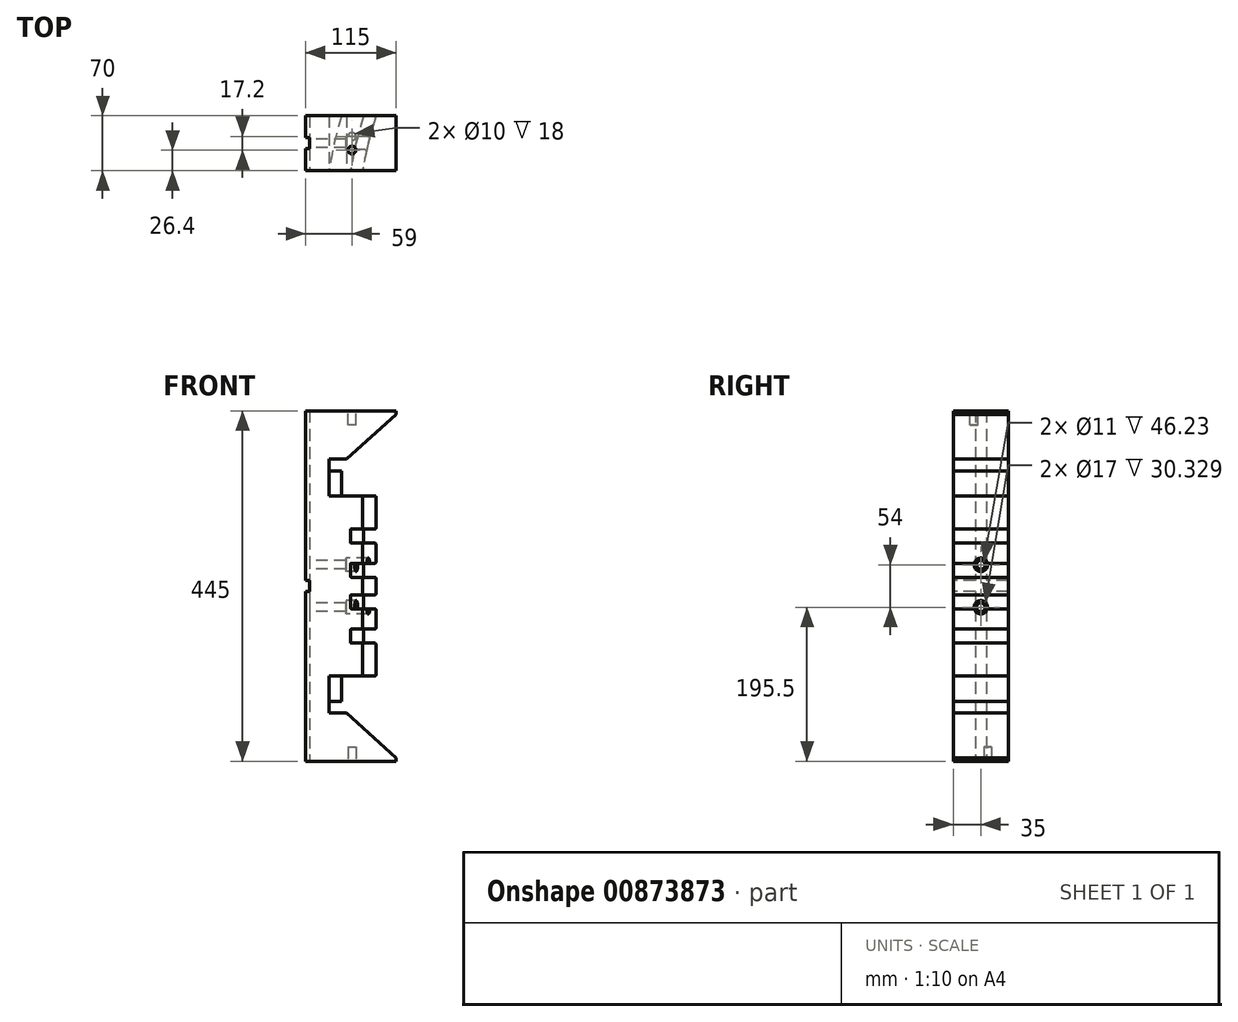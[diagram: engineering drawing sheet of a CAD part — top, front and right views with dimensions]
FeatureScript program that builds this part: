
annotation { "Feature Type Name" : "Feature", "Feature Type Description" : "" }
export const myFeature = defineFeature(function(context is Context, id is Id, definition is map)
    precondition{}
    {
        {
            var Q0;
            Q0=qCreatedBy(makeId("Top.planeOp"),FACE);
            var sketch = newSketch(context, id + "F0", { "sketchPlane" : qUnion([Q0])});
            skArc(sketch, "E0", {"start": v(-433.01, 250) * mm, "mid": v(-482.96, 129.4) * mm, "end": v(-500, 0) * mm});
            skLineSegment(sketch, "E1", {"start": v(0, 0) * mm, "end": v(-433.01, 250) * mm, "construction": true});
            skLineSegment(sketch, "E2", {"start": v(0, 0) * mm, "end": v(-500, 0) * mm, "construction": true});
            skSolve(sketch);
        }
        {
            var Q0;
            Q0=qCreatedBy(makeId("Front.planeOp"),FACE);
            var sketch = newSketch(context, id + "F1", { "sketchPlane" : qUnion([Q0])});
            skLineSegment(sketch, "E3", {"start": v(-500, 0) * mm, "end": v(-500, 9.2) * mm});
            skLineSegment(sketch, "E4", {"start": v(-502, 11.2) * mm, "end": v(-514, 11.2) * mm});
            skLineSegment(sketch, "E5", {"start": v(-515, 12.2) * mm, "end": v(-515, 27.9) * mm});
            skLineSegment(sketch, "E6", {"start": v(-514, 28.9) * mm, "end": v(-502, 28.9) * mm});
            skLineSegment(sketch, "E7", {"start": v(-502, 72.44) * mm, "end": v(-514, 72.44) * mm});
            skLineSegment(sketch, "E8", {"start": v(-515, 55.66) * mm, "end": v(-515, 71.44) * mm});
            skLineSegment(sketch, "E9", {"start": v(-514, 54.66) * mm, "end": v(-502.1, 54.66) * mm});
            skLineSegment(sketch, "E10", {"start": v(-502, 114.4) * mm, "end": v(-542, 114.4) * mm});
            skLineSegment(sketch, "E11", {"start": v(-542, 114.4) * mm, "end": v(-542, 146.4) * mm});
            skLineSegment(sketch, "E12", {"start": v(-542, 146.4) * mm, "end": v(-565, 146.4) * mm});
            skLineSegment(sketch, "E13", {"start": v(-565, 146.4) * mm, "end": v(-565, 0) * mm});
            skLineSegment(sketch, "E14", {"start": v(-515, 63.55) * mm, "end": v(-448.96, 63.55) * mm, "construction": true});
            skLineSegment(sketch, "E15", {"start": v(-515, 20.05) * mm, "end": v(-458.8, 20.05) * mm, "construction": true});
            skLineSegment(sketch, "E16", {"start": v(-500, 112.4) * mm, "end": v(-500, 74.44) * mm});
            skLineSegment(sketch, "E17", {"start": v(-500, 52.56) * mm, "end": v(-500, 30.9) * mm});
            skPoint(sketch, "E18.visualSharp", {"position": v(-515, 72.44) * mm});
            skArc(sketch, "E18.filletArc", {"start": v(-514, 72.44) * mm, "mid": v(-514.7, 72.15) * mm, "end": v(-515, 71.44) * mm});
            skPoint(sketch, "E19.visualSharp", {"position": v(-515, 54.66) * mm});
            skArc(sketch, "E19.filletArc", {"start": v(-515, 55.66) * mm, "mid": v(-514.7, 54.95) * mm, "end": v(-514, 54.66) * mm});
            skPoint(sketch, "E20.visualSharp", {"position": v(-515, 28.9) * mm});
            skArc(sketch, "E20.filletArc", {"start": v(-514, 28.9) * mm, "mid": v(-514.7, 28.6) * mm, "end": v(-515, 27.9) * mm});
            skPoint(sketch, "E21.visualSharp", {"position": v(-515, 11.2) * mm});
            skArc(sketch, "E21.filletArc", {"start": v(-515, 12.2) * mm, "mid": v(-514.7, 11.5) * mm, "end": v(-514, 11.2) * mm});
            skPoint(sketch, "E22.visualSharp", {"position": v(-500, 11.2) * mm});
            skArc(sketch, "E22.filletArc", {"start": v(-500, 9.2) * mm, "mid": v(-500.59, 10.61) * mm, "end": v(-502, 11.2) * mm});
            skPoint(sketch, "E23.visualSharp", {"position": v(-500, 28.9) * mm});
            skArc(sketch, "E23.filletArc", {"start": v(-502, 28.9) * mm, "mid": v(-500.59, 29.49) * mm, "end": v(-500, 30.9) * mm});
            skPoint(sketch, "E24.visualSharp", {"position": v(-500, 54.66) * mm});
            skArc(sketch, "E24.filletArc", {"start": v(-500, 52.56) * mm, "mid": v(-500.62, 54.04) * mm, "end": v(-502.1, 54.66) * mm});
            skPoint(sketch, "E25.visualSharp", {"position": v(-500, 72.44) * mm});
            skArc(sketch, "E25.filletArc", {"start": v(-502, 72.44) * mm, "mid": v(-500.59, 73.03) * mm, "end": v(-500, 74.44) * mm});
            skPoint(sketch, "E26.visualSharp", {"position": v(-500, 114.4) * mm});
            skArc(sketch, "E26.filletArc", {"start": v(-500, 112.4) * mm, "mid": v(-500.59, 113.81) * mm, "end": v(-502, 114.4) * mm});
            skArc(sketch, "E27.MirrorCS", {"start": v(-500, -9.2) * mm, "mid": v(-500.59, -10.61) * mm, "end": v(-502, -11.2) * mm});
            skLineSegment(sketch, "E28.MirrorCS", {"start": v(-502, -11.2) * mm, "end": v(-514, -11.2) * mm});
            skLineSegment(sketch, "E29.MirrorCS", {"start": v(-502, -72.44) * mm, "end": v(-514, -72.44) * mm});
            skArc(sketch, "E30.MirrorCS", {"start": v(-502, -72.44) * mm, "mid": v(-500.59, -73.03) * mm, "end": v(-500, -74.44) * mm});
            skArc(sketch, "E31.MirrorCS", {"start": v(-514, -72.44) * mm, "mid": v(-514.7, -72.15) * mm, "end": v(-515, -71.44) * mm});
            skArc(sketch, "E32.MirrorCS", {"start": v(-515, -12.2) * mm, "mid": v(-514.7, -11.5) * mm, "end": v(-514, -11.2) * mm});
            skArc(sketch, "E33.MirrorCS", {"start": v(-514, -28.9) * mm, "mid": v(-514.7, -28.6) * mm, "end": v(-515, -27.9) * mm});
            skArc(sketch, "E34.MirrorCS", {"start": v(-500, -112.4) * mm, "mid": v(-500.59, -113.81) * mm, "end": v(-502, -114.4) * mm});
            skLineSegment(sketch, "E35.MirrorCS", {"start": v(-514, -54.66) * mm, "end": v(-502.1, -54.66) * mm});
            skLineSegment(sketch, "E36.MirrorCS", {"start": v(-515, -55.66) * mm, "end": v(-515, -71.44) * mm});
            skArc(sketch, "E37.MirrorCS", {"start": v(-502, -28.9) * mm, "mid": v(-500.59, -29.49) * mm, "end": v(-500, -30.9) * mm});
            skLineSegment(sketch, "E38.MirrorCS", {"start": v(-514, -28.9) * mm, "end": v(-502, -28.9) * mm});
            skArc(sketch, "E39.MirrorCS", {"start": v(-500, -52.56) * mm, "mid": v(-500.62, -54.04) * mm, "end": v(-502.1, -54.66) * mm});
            skArc(sketch, "E40.MirrorCS", {"start": v(-515, -55.66) * mm, "mid": v(-514.7, -54.95) * mm, "end": v(-514, -54.66) * mm});
            skLineSegment(sketch, "E41.MirrorCS", {"start": v(-515, -12.2) * mm, "end": v(-515, -27.9) * mm});
            skPoint(sketch, "E42.MirrorP", {"position": v(-500, -11.2) * mm});
            skPoint(sketch, "E43.MirrorP", {"position": v(-500, -72.44) * mm});
            skPoint(sketch, "E44.MirrorP", {"position": v(-515, -11.2) * mm});
            skPoint(sketch, "E45.MirrorP", {"position": v(-500, -28.9) * mm});
            skPoint(sketch, "E46.MirrorP", {"position": v(-500, -54.66) * mm});
            skLineSegment(sketch, "E47.MirrorCS", {"start": v(-500, -52.56) * mm, "end": v(-500, -30.9) * mm});
            skPoint(sketch, "E48.MirrorP", {"position": v(-515, -72.44) * mm});
            skPoint(sketch, "E49.MirrorP", {"position": v(-515, -28.9) * mm});
            skLineSegment(sketch, "E50.MirrorCS", {"start": v(-542, -114.4) * mm, "end": v(-542, -146.4) * mm});
            skPoint(sketch, "E51.MirrorP", {"position": v(-500, -114.4) * mm});
            skLineSegment(sketch, "E52.MirrorCS", {"start": v(-500, -112.4) * mm, "end": v(-500, -74.44) * mm});
            skLineSegment(sketch, "E53.MirrorCS", {"start": v(-542, -146.4) * mm, "end": v(-565, -146.4) * mm});
            skLineSegment(sketch, "E54.MirrorCS", {"start": v(-502, -114.4) * mm, "end": v(-542, -114.4) * mm});
            skLineSegment(sketch, "E55.MirrorCS", {"start": v(-515, -63.55) * mm, "end": v(-448.96, -63.55) * mm, "construction": true});
            skLineSegment(sketch, "E56.MirrorCS", {"start": v(-515, -20.05) * mm, "end": v(-458.8, -20.05) * mm, "construction": true});
            skLineSegment(sketch, "E57.MirrorCS", {"start": v(-565, -146.4) * mm, "end": v(-565, 0) * mm});
            skPoint(sketch, "E58.MirrorP", {"position": v(-515, -54.66) * mm});
            skLineSegment(sketch, "E59", {"start": v(-500, -9.2) * mm, "end": v(-500, 0) * mm});
            skSolve(sketch);
        }
        {
            var Q0;
            Q0=makeQuery(id+"F1.imprint","IMPRINT",FACE,{"disambiguationData":[TD([[makeQuery(id+"F1.imprint","IMPRINT",EDGE,{"derivedFrom":sQuery(id+"F1.wireOp",EDGE,"E3")}),1.0]])]});
            var Q1;
            Q1=sQuery(id+"F0.wireOp",EDGE,"E0");
            sweep(context, id + "F2", {"profiles" : qUnion([Q0]), "path" : qUnion([Q1])});
        }
        {
            var Q0;
            Q0=makeQuery(id+"F2.opSweep","SWEPT_FACE",FACE,{"disambiguationData":[OSD([sQuery(id+"F0.wireOp",EDGE,"E0"),sQuery(id+"F1.wireOp",EDGE,"E12")])]});
            var sketch = newSketch(context, id + "F3", { "sketchPlane" : qUnion([Q0])});
            skLineSegment(sketch, "E60", {"start": v(0, 0) * mm, "end": v(-565, 0) * mm});
            skLineSegment(sketch, "E61", {"start": v(-565, 85) * mm, "end": v(-565, 155) * mm});
            skLineSegment(sketch, "E62", {"start": v(-565, 85) * mm, "end": v(-558.57, 85) * mm});
            skLineSegment(sketch, "E63", {"start": v(-543.32, 155) * mm, "end": v(-565, 155) * mm});
            skArc(sketch, "E64", {"start": v(-543.32, 155) * mm, "mid": v(-552.06, 120.24) * mm, "end": v(-558.57, 85) * mm});
            skSolve(sketch);
        }
        {
            var Q0;
            Q0=makeQuery(id+"F3.imprint","IMPRINT",FACE,{"disambiguationData":[TD([[makeQuery(id+"F3.imprint","IMPRINT",EDGE,{"derivedFrom":sQuery(id+"F3.wireOp",EDGE,"E61")}),-1.0]])]});
            var Q1;
            Q1=makeQuery(id+"F2.opSweep","SWEPT_FACE",FACE,{"disambiguationData":[OSD([sQuery(id+"F0.wireOp",EDGE,"E0"),sQuery(id+"F1.wireOp",EDGE,"E53.MirrorCS")])]});
            extrude(context, id + "F4", {"entities" : qUnion([Q0]), "operationType" : NewBodyOperationType.ADD, "endBound" : BoundingType.UP_TO_SURFACE, "oppositeDirection" : true, "depth" : 25 * mm, "endBoundEntityFace" : qUnion([Q1]), "offsetDistance" : 25 * mm});
        }
        {
            var Q0;
            Q0=makeQuery(id+"F4.boolean.opBoolean","MERGE",FACE,{"derivedFrom":[makeQuery(id+"F2.opSweep","SWEPT_FACE",FACE,{"disambiguationData":[OSD([sQuery(id+"F0.wireOp",EDGE,"E0"),sQuery(id+"F1.wireOp",EDGE,"E12")])]}),makeQuery(id+"F4.opExtrude","CAP_FACE",FACE,{"disambiguationData":[OSD([sQuery(id+"F3.wireOp",EDGE,"E61"),sQuery(id+"F3.wireOp",EDGE,"E62"),sQuery(id+"F3.wireOp",EDGE,"E63"),sQuery(id+"F3.wireOp",EDGE,"E64")])],"isStart":true})]});
            var sketch = newSketch(context, id + "F5", { "sketchPlane" : qUnion([Q0])});
            skLineSegment(sketch, "E65", {"start": v(-543.32, 155) * mm, "end": v(-475.37, 155) * mm});
            skLineSegment(sketch, "E66", {"start": v(-558.57, 85) * mm, "end": v(-492.72, 85) * mm});
            skLineSegment(sketch, "E67", {"start": v(-489.3, 282.5) * mm, "end": v(-433.01, 250) * mm});
            skLineSegment(sketch, "E68", {"start": v(-565, 0) * mm, "end": v(-500, 0) * mm});
            skArc(sketch, "E69", {"start": v(-489.3, 282.5) * mm, "mid": v(-520.23, 220.41) * mm, "end": v(-543.32, 155) * mm});
            skArc(sketch, "E70", {"start": v(-433.01, 250) * mm, "mid": v(-456.67, 203.6) * mm, "end": v(-475.37, 155) * mm});
            skArc(sketch, "E71.trimOffspring", {"start": v(-492.72, 85) * mm, "mid": v(-498.18, 42.66) * mm, "end": v(-500, 0) * mm});
            skArc(sketch, "E72.trimOffspring", {"start": v(-558.57, 85) * mm, "mid": v(-563.4, 42.62) * mm, "end": v(-565, 0) * mm});
            skSolve(sketch);
        }
        {
            var Q0;
            {var subQ0=sQuery(id+"F5.wireOp",EDGE,"E71.trimOffspring");Q0=makeQuery(id+"F5.imprint","IMPRINT",FACE,{"disambiguationData":[TD([[makeQuery(id+"F5.imprint","IMPRINT",EDGE,{"derivedFrom":subQ0}),-1.0]])]});}
            var Q1;
            {var subQ0=sQuery(id+"F5.wireOp",EDGE,"E72.trimOffspring");Q1=makeQuery(id+"F5.imprint","IMPRINT",FACE,{"disambiguationData":[TD([[makeQuery(id+"F5.imprint","IMPRINT",EDGE,{"derivedFrom":subQ0}),-1.0]])]});}
            var Q2;
            {var subQ0=sQuery(id+"F5.wireOp",EDGE,"E69");Q2=makeQuery(id+"F5.imprint","IMPRINT",FACE,{"disambiguationData":[TD([[makeQuery(id+"F5.imprint","IMPRINT",EDGE,{"derivedFrom":subQ0}),-1.0]])]});}
            var Q3;
            {var subQ0=sQuery(id+"F5.wireOp",EDGE,"E70");Q3=makeQuery(id+"F5.imprint","IMPRINT",FACE,{"disambiguationData":[TD([[makeQuery(id+"F5.imprint","IMPRINT",EDGE,{"derivedFrom":subQ0}),-1.0]])]});}
            var Q4;
            Q4=makeQuery(id+"F4.boolean.opBoolean","MERGE",FACE,{"derivedFrom":[makeQuery(id+"F2.opSweep","SWEPT_FACE",FACE,{"disambiguationData":[OSD([sQuery(id+"F0.wireOp",EDGE,"E0"),sQuery(id+"F1.wireOp",EDGE,"E53.MirrorCS")])]}),makeQuery(id+"F4.opExtrude","CAP_FACE",FACE,{"disambiguationData":[OSD([sQuery(id+"F3.wireOp",EDGE,"E61"),sQuery(id+"F3.wireOp",EDGE,"E62"),sQuery(id+"F3.wireOp",EDGE,"E63"),sQuery(id+"F3.wireOp",EDGE,"E64")])],"isStart":false})]});
            extrude(context, id + "F6", {"entities" : qUnion([Q0, Q1, Q2, Q3]), "operationType" : NewBodyOperationType.REMOVE, "endBound" : BoundingType.UP_TO_SURFACE, "oppositeDirection" : true, "depth" : 25 * mm, "endBoundEntityFace" : qUnion([Q4]), "offsetDistance" : 25 * mm});
        }
        {
            var Q0;
            Q0=makeQuery(id+"F6.boolean.opBoolean","MERGE",FACE,{"derivedFrom":[makeQuery(id+"F4.opExtrude","SWEPT_FACE",FACE,{"disambiguationData":[OSD([sQuery(id+"F3.wireOp",EDGE,"E62")])]})],"fromTools":[makeQuery(id+"F6.opExtrude","SWEPT_FACE",FACE,{"disambiguationData":[OSD([sQuery(id+"F5.wireOp",EDGE,"E66")])]})]});
            var sketch = newSketch(context, id + "F7", { "sketchPlane" : qUnion([Q0])});
            skLineSegment(sketch, "E73", {"start": v(-565, 146.4) * mm, "end": v(-565, 222.5) * mm});
            skLineSegment(sketch, "E74", {"start": v(-565, 222.5) * mm, "end": v(-445, 222.5) * mm, "construction": true});
            skLineSegment(sketch, "E75", {"start": v(-445, 222.5) * mm, "end": v(-512.86, 161.4) * mm, "construction": true});
            skLineSegment(sketch, "E76", {"start": v(-512.86, 161.4) * mm, "end": v(-535.3, 161.4) * mm});
            skLineSegment(sketch, "E77", {"start": v(-535.3, 161.4) * mm, "end": v(-535.3, 146.4) * mm});
            skLineSegment(sketch, "E78", {"start": v(-535.3, 146.4) * mm, "end": v(-565, 146.4) * mm});
            skLineSegment(sketch, "E79", {"start": v(-565, 222.5) * mm, "end": v(-450, 222.5) * mm});
            skLineSegment(sketch, "E80", {"start": v(-450, 222.5) * mm, "end": v(-450, 218) * mm});
            skLineSegment(sketch, "E81", {"start": v(-512.86, 161.4) * mm, "end": v(-450, 218) * mm});
            skLineSegment(sketch, "E82.MirrorCS", {"start": v(-450, -222.5) * mm, "end": v(-450, -218) * mm});
            skLineSegment(sketch, "E83.MirrorCS", {"start": v(-535.3, -161.4) * mm, "end": v(-535.3, -146.4) * mm});
            skLineSegment(sketch, "E84.MirrorCS", {"start": v(-535.3, -146.4) * mm, "end": v(-565, -146.4) * mm});
            skLineSegment(sketch, "E85.MirrorCS", {"start": v(-512.86, -161.4) * mm, "end": v(-535.3, -161.4) * mm});
            skLineSegment(sketch, "E86.MirrorCS", {"start": v(-565, -222.5) * mm, "end": v(-450, -222.5) * mm});
            skLineSegment(sketch, "E87.MirrorCS", {"start": v(-512.86, -161.4) * mm, "end": v(-450, -218) * mm});
            skLineSegment(sketch, "E88.MirrorCS", {"start": v(-565, -222.5) * mm, "end": v(-445, -222.5) * mm, "construction": true});
            skLineSegment(sketch, "E89.MirrorCS", {"start": v(-445, -222.5) * mm, "end": v(-512.86, -161.4) * mm, "construction": true});
            skLineSegment(sketch, "E90.MirrorCS", {"start": v(-565, -146.4) * mm, "end": v(-565, -222.5) * mm});
            skSolve(sketch);
        }
        {
            var Q0;
            Q0=makeQuery(id+"F7.imprint","IMPRINT",FACE,{"disambiguationData":[TD([[makeQuery(id+"F7.imprint","IMPRINT",EDGE,{"derivedFrom":sQuery(id+"F7.wireOp",EDGE,"E82.MirrorCS")}),1.0]])]});
            var Q1;
            Q1=makeQuery(id+"F7.imprint","IMPRINT",FACE,{"disambiguationData":[TD([[makeQuery(id+"F7.imprint","IMPRINT",EDGE,{"derivedFrom":sQuery(id+"F7.wireOp",EDGE,"E73")}),-1.0]])]});
            var Q2;
            Q2=makeQuery(id+"F6.boolean.opBoolean","MERGE",FACE,{"derivedFrom":[makeQuery(id+"F4.opExtrude","SWEPT_FACE",FACE,{"disambiguationData":[OSD([sQuery(id+"F3.wireOp",EDGE,"E63")])]})],"fromTools":[makeQuery(id+"F6.opExtrude","SWEPT_FACE",FACE,{"disambiguationData":[OSD([sQuery(id+"F5.wireOp",EDGE,"E65")])]})]});
            extrude(context, id + "F8", {"entities" : qUnion([Q0, Q1]), "operationType" : NewBodyOperationType.ADD, "endBound" : BoundingType.UP_TO_SURFACE, "oppositeDirection" : true, "depth" : 25 * mm, "endBoundEntityFace" : qUnion([Q2]), "offsetDistance" : 25 * mm});
        }
        {
            var Q0;
            Q0=makeQuery(id+"F8.boolean.opBoolean","MERGE",FACE,{"derivedFrom":[makeQuery(id+"F4.opExtrude","SWEPT_FACE",FACE,{"disambiguationData":[OSD([sQuery(id+"F3.wireOp",EDGE,"E61")])]}),makeQuery(id+"F8.opExtrude","SWEPT_FACE",FACE,{"disambiguationData":[OSD([sQuery(id+"F7.wireOp",EDGE,"E73")])]}),makeQuery(id+"F8.opExtrude","SWEPT_FACE",FACE,{"disambiguationData":[OSD([sQuery(id+"F7.wireOp",EDGE,"E90.MirrorCS")])]})]});
            var sketch = newSketch(context, id + "F9", { "sketchPlane" : qUnion([Q0])});
            skLineSegment(sketch, "E91.bottom", {"start": v(-127, 222.5) * mm, "end": v(-113, 222.5) * mm});
            skLineSegment(sketch, "E91.top", {"start": v(-127, -222.5) * mm, "end": v(-113, -222.5) * mm});
            skLineSegment(sketch, "E91.left", {"start": v(-127, 222.5) * mm, "end": v(-127, 7) * mm});
            skLineSegment(sketch, "E91.right", {"start": v(-113, 222.5) * mm, "end": v(-113, 7) * mm});
            skLineSegment(sketch, "E92.bottom", {"start": v(-155, 7) * mm, "end": v(-127, 7) * mm});
            skLineSegment(sketch, "E92.top", {"start": v(-155, -7) * mm, "end": v(-127, -7) * mm});
            skLineSegment(sketch, "E92.left", {"start": v(-155, 7) * mm, "end": v(-155, -7) * mm});
            skLineSegment(sketch, "E92.right", {"start": v(-85, 7) * mm, "end": v(-85, -7) * mm});
            skLineSegment(sketch, "E93.trimOffspring", {"start": v(-113, 7) * mm, "end": v(-85, 7) * mm});
            skLineSegment(sketch, "E94.trimOffspring", {"start": v(-113, -7) * mm, "end": v(-113, -222.5) * mm});
            skLineSegment(sketch, "E95.trimOffspring", {"start": v(-113, -7) * mm, "end": v(-85, -7) * mm});
            skLineSegment(sketch, "E96.trimOffspring", {"start": v(-127, -7) * mm, "end": v(-127, -222.5) * mm});
            skSolve(sketch);
        }
        {
            var Q0;
            Q0 = qSketchRegion(id + "F9", true);
            extrude(context, id + "F10", {"entities" : qUnion([Q0]), "operationType" : NewBodyOperationType.REMOVE, "oppositeDirection" : true, "depth" : 5 * mm, "offsetDistance" : 25 * mm});
        }
        {
            var Q0;
            Q0=makeQuery(id+"F10.boolean.opBoolean","COPY",FACE,{"derivedFrom":makeQuery(id+"F10.opExtrude","CAP_FACE",FACE,{"disambiguationData":[OSD([sQuery(id+"F9.wireOp",EDGE,"E91.bottom"),sQuery(id+"F9.wireOp",EDGE,"E91.top"),sQuery(id+"F9.wireOp",EDGE,"E91.left"),sQuery(id+"F9.wireOp",EDGE,"E91.right"),sQuery(id+"F9.wireOp",EDGE,"E92.bottom"),sQuery(id+"F9.wireOp",EDGE,"E92.top"),sQuery(id+"F9.wireOp",EDGE,"E92.left"),sQuery(id+"F9.wireOp",EDGE,"E92.right"),sQuery(id+"F9.wireOp",EDGE,"E93.trimOffspring"),sQuery(id+"F9.wireOp",EDGE,"E94.trimOffspring"),sQuery(id+"F9.wireOp",EDGE,"E95.trimOffspring"),sQuery(id+"F9.wireOp",EDGE,"E96.trimOffspring")])],"isStart":false})});
            var sketch = newSketch(context, id + "F11", { "sketchPlane" : qUnion([Q0])});
            skCircle(sketch, "E97", {"center": v(-120, 27) * mm, "radius": 5.5 * mm});
            skCircle(sketch, "E98", {"center": v(-120, -27) * mm, "radius": 5.5 * mm});
            skSolve(sketch);
        }
        {
            var Q0;
            Q0 = qSketchRegion(id + "F11", true);
            var Q1;
            Q1=makeQuery(id+"F2.opSweep","SWEPT_FACE",FACE,{"disambiguationData":[OSD([sQuery(id+"F0.wireOp",EDGE,"E0"),sQuery(id+"F1.wireOp",EDGE,"E3"),sQuery(id+"F1.wireOp",EDGE,"E59")])]});
            extrude(context, id + "F12", {"entities" : qUnion([Q0]), "operationType" : NewBodyOperationType.REMOVE, "endBound" : BoundingType.UP_TO_SURFACE, "oppositeDirection" : true, "depth" : 25 * mm, "endBoundEntityFace" : qUnion([Q1]), "offsetDistance" : 25 * mm});
        }
        {
            var Q0;
            Q0=qCreatedBy(makeId("Right.planeOp"),FACE);
            cPlane(context, id + "F13", {"entities" : qUnion([Q0]), "cplaneType" : CPlaneType.OFFSET, "offset" : (526 - 12.23) * mm, "oppositeDirection" : true, "width" : 150 * mm, "height" : 150 * mm});
        }
        {
            var Q0;
            Q0=qCreatedBy(id+"F13.planeOp",FACE);
            var sketch = newSketch(context, id + "F14", { "sketchPlane" : qUnion([Q0])});
            skCircle(sketch, "E99", {"center": v(120, 27) * mm, "radius": 8.5 * mm});
            skCircle(sketch, "E100", {"center": v(120, -27) * mm, "radius": 8.5 * mm});
            skSolve(sketch);
        }
        {
            var Q0;
            Q0 = qSketchRegion(id + "F14", true);
            var Q1;
            Q1=makeQuery(id+"F2.opSweep","SWEPT_FACE",FACE,{"disambiguationData":[OSD([sQuery(id+"F0.wireOp",EDGE,"E0"),sQuery(id+"F1.wireOp",EDGE,"E3"),sQuery(id+"F1.wireOp",EDGE,"E59")])]});
            extrude(context, id + "F15", {"entities" : qUnion([Q0]), "operationType" : NewBodyOperationType.REMOVE, "endBound" : BoundingType.UP_TO_SURFACE, "depth" : 25 * mm, "endBoundEntityFace" : qUnion([Q1]), "offsetDistance" : 25 * mm});
        }
        {
            var Q0;
            Q0=makeQuery(id+"F8.opExtrude","SWEPT_FACE",FACE,{"disambiguationData":[OSD([sQuery(id+"F7.wireOp",EDGE,"E79")])]});
            var sketch = newSketch(context, id + "F16", { "sketchPlane" : qUnion([Q0])});
            skCircle(sketch, "E101", {"center": v(-506, 111.4) * mm, "radius": 5 * mm});
            skSolve(sketch);
        }
        {
            var Q0;
            Q0 = qSketchRegion(id + "F16", true);
            extrude(context, id + "F17", {"entities" : qUnion([Q0]), "operationType" : NewBodyOperationType.REMOVE, "oppositeDirection" : true, "depth" : 18 * mm, "offsetDistance" : 25 * mm});
        }
        {
            var Q0;
            Q0=makeQuery(id+"F8.opExtrude","SWEPT_FACE",FACE,{"disambiguationData":[OSD([sQuery(id+"F7.wireOp",EDGE,"E86.MirrorCS")])]});
            var sketch = newSketch(context, id + "F18", { "sketchPlane" : qUnion([Q0])});
            skCircle(sketch, "E102", {"center": v(-506, -128.6) * mm, "radius": 5 * mm});
            skSolve(sketch);
        }
        {
            var Q0;
            Q0=makeQuery(id+"F18.imprint","IMPRINT",FACE,{"disambiguationData":[TD([[makeQuery(id+"F18.imprint","IMPRINT",EDGE,{"derivedFrom":sQuery(id+"F18.wireOp",EDGE,"E102")}),1.0]])]});
            extrude(context, id + "F19", {"entities" : qUnion([Q0]), "operationType" : NewBodyOperationType.REMOVE, "oppositeDirection" : true, "depth" : 18 * mm, "offsetDistance" : 25 * mm});
        }
    });
